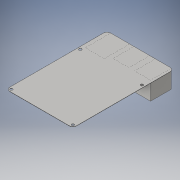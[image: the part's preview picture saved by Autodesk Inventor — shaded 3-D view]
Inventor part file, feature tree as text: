
AUTODESK INVENTOR PART (.ipt)
format: ipt  version: 2016 (Build 200138000, 138)  size: 147,456 bytes
history: native  units: in
note: dims shown in document units (in); Inventor stores cm internally (conversion verified against a paired STEP export)
features: extrude x3, sketch x3, fillet x1
ambient origin geometry x8: Origin, YZ Plane, XZ Plane, XY Plane, X Axis, Y Axis, Z Axis, Center Point
bodies: Solid1 (feature_tree)
feature tree (7):
  extrude  "Extrusion1"  Depth=3.338in
  fillet  "Fillet1"  Radius=0.0077in
  extrude  "Extrusion2"  Depth=0.086in
  extrude  "Extrusion3"  Depth=0.086in
  sketch  "Sketch1"  dims[d0=2.208in d1=3.338in d2=0.0077in d3=0.0in]
  sketch  "Sketch2"  dims[d4=0.125in d5=0.086in]
  sketch  "Sketch3"  dims[d6=0.086in d7=0.086in d8=0.086in d9=2.195in d10=2.195in d11=0.0077in d12=0.0in d13=0.527in d14=0.527in d16=0.685in d18=0.837in d19=0.627in d20=0.0in d21=0.0in d22=0.185in d23=0.141in d24=0.086in d25=0.6in d26=0.0in]
